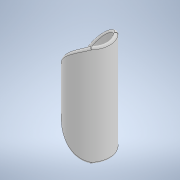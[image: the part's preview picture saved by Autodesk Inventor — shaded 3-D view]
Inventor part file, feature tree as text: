
AUTODESK INVENTOR PART (.ipt)
format: ipt  version: 2020 (Build 240168000, 168)  size: 352,768 bytes
history: native  units: in
note: dims shown in document units (in); Inventor stores cm internally (conversion verified against a paired STEP export)
features: extrude x4, sketch x4, fillet x2
ambient origin geometry x8: Origin, YZ Plane, XZ Plane, XY Plane, X Axis, Y Axis, Z Axis, Center Point
bodies: Solid1 (feature_tree)
feature tree (10):
  extrude  "Extrusion1"  Depth=0.6in
  extrude  "Extrusion2"  TaperAngle=0.0deg  [1 undecoded]
  sketch  "Sketch3"  dims[d5=0.1in d6=90.0deg]
  extrude  "Extrusion3"  TaperAngle=90.0deg  [1 undecoded]
  extrude  "Extrusion4"  Depth=0.025in
  fillet  "Fillet1"  [1 undecoded]
  fillet  "Fillet2"  Radius=0.5in
  sketch  "Sketch1"  dims[d0=0.6in d1=0.6in]
  sketch  "Sketch2"  dims[d2=1.5in d3=0.0in d4=0.0in]
  sketch  "Sketch4"  dims[d7=0.6in d8=0.0in d9=0.3in d10=180.0deg d11=0.5in d12=0.6in d13=0.06in d14=0.12in d15=0.1in d16=0.0in d17=1.5in d18=0.0in d19=0.025in d20=0.025in]
note: 3 required parameter values undecoded (feature->parameter linkage not recoverable at this tier; creation-order binding heuristic only, values carry confidence <= 0.55)
